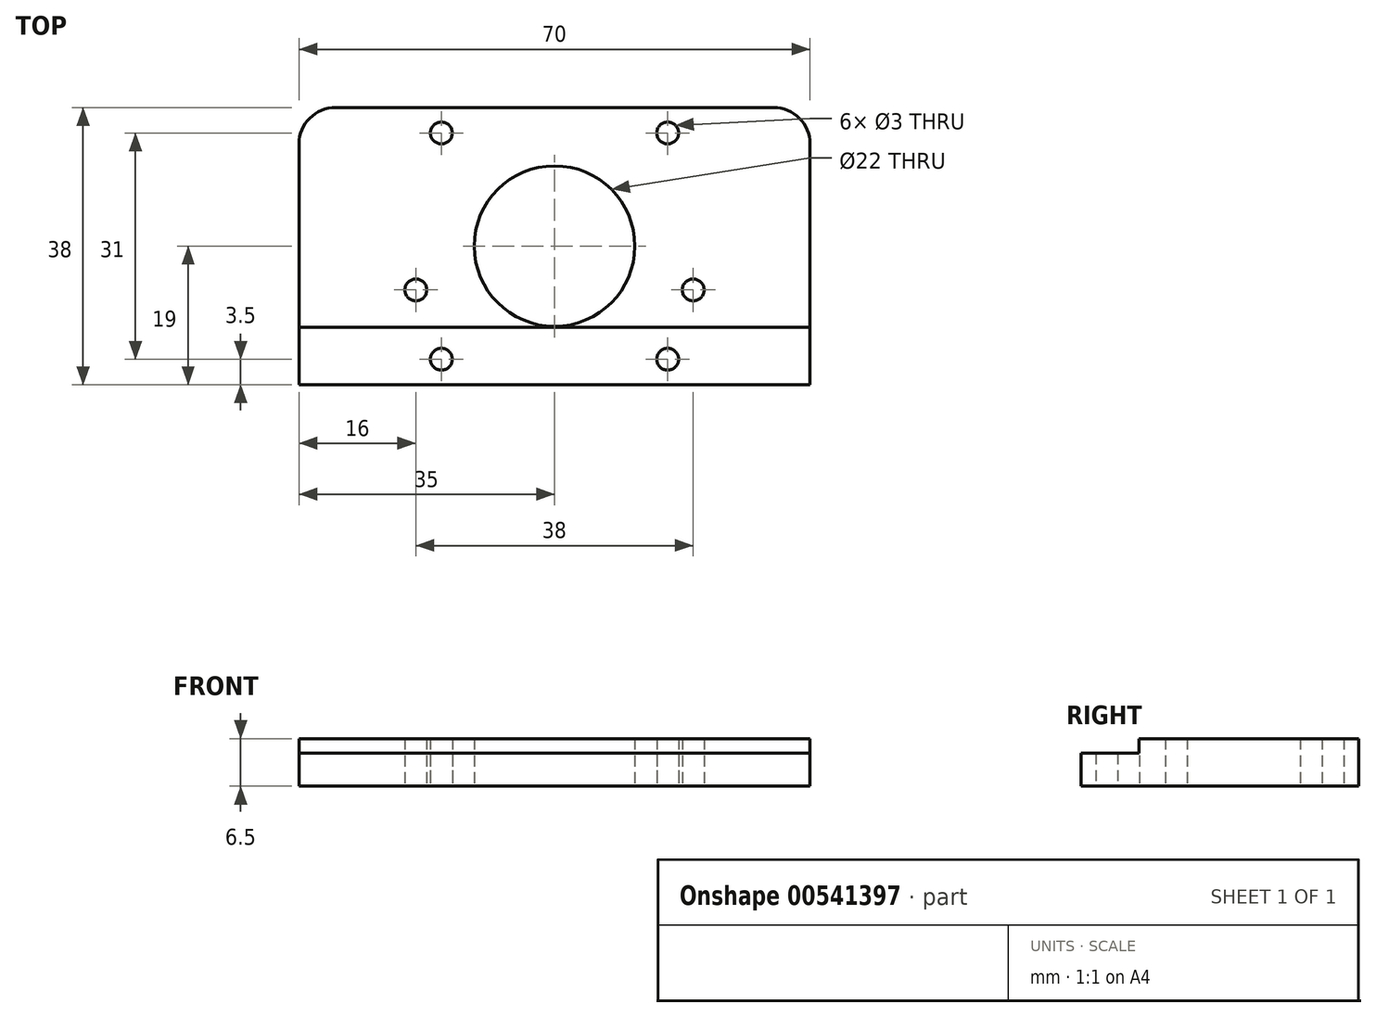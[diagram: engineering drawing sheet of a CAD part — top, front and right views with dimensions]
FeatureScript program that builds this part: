
annotation { "Feature Type Name" : "Feature", "Feature Type Description" : "" }
export const myFeature = defineFeature(function(context is Context, id is Id, definition is map)
    precondition{}
    {
        {
            var Q0;
            Q0=qCreatedBy(makeId("Top.planeOp"),FACE);
            var sketch = newSketch(context, id + "F0", { "sketchPlane" : qUnion([Q0])});
            skLineSegment(sketch, "E0.bottom", {"start": v(35, 19) * mm, "end": v(-35, 19) * mm});
            skLineSegment(sketch, "E0.top", {"start": v(35, -19) * mm, "end": v(-35, -19) * mm});
            skLineSegment(sketch, "E0.left", {"start": v(35, 19) * mm, "end": v(35, -19) * mm});
            skLineSegment(sketch, "E0.right", {"start": v(-35, 19) * mm, "end": v(-35, -19) * mm});
            skCircle(sketch, "E1", {"center": v(-15.5, 15.5) * mm, "radius": 1.5 * mm});
            skCircle(sketch, "E2", {"center": v(15.5, 15.5) * mm, "radius": 1.5 * mm});
            skCircle(sketch, "E3", {"center": v(-15.5, -15.5) * mm, "radius": 1.5 * mm});
            skCircle(sketch, "E4", {"center": v(15.5, -15.5) * mm, "radius": 1.5 * mm});
            skCircle(sketch, "E5", {"center": v(19, -6) * mm, "radius": 1.5 * mm});
            skCircle(sketch, "E6", {"center": v(-19, -6) * mm, "radius": 1.5 * mm});
            skCircle(sketch, "E7", {"center": v(0, 0) * mm, "radius": 11 * mm});
            skLineSegment(sketch, "E8", {"start": v(-15.5, 15.5) * mm, "end": v(15.5, 15.5) * mm, "construction": true});
            skLineSegment(sketch, "E9", {"start": v(-15.5, 15.5) * mm, "end": v(-15.5, -15.5) * mm, "construction": true});
            skLineSegment(sketch, "E10", {"start": v(15.5, -15.5) * mm, "end": v(-15.5, -15.5) * mm, "construction": true});
            skLineSegment(sketch, "E11", {"start": v(15.5, 15.5) * mm, "end": v(15.5, -15.5) * mm, "construction": true});
            skPoint(sketch, "E12.endSnap0", {"position": v(0, -19) * mm});
            skSolve(sketch);
        }
        {
            var Q0;
            Q0=makeQuery(id+"F0.imprint","IMPRINT",FACE,{"disambiguationData":[TD([[makeQuery(id+"F0.imprint","IMPRINT",EDGE,{"derivedFrom":sQuery(id+"F0.wireOp",EDGE,"E0.bottom")}),1.0]])]});
            var Q1;
            Q1=sQuery(id+"F0.wireOp",EDGE,"E0.bottom");
            var Q2;
            Q2=sQuery(id+"F0.wireOp",EDGE,"E0.right");
            var Q3;
            Q3=sQuery(id+"F0.wireOp",EDGE,"E0.top");
            var Q4;
            Q4=sQuery(id+"F0.wireOp",EDGE,"E0.left");
            extrude(context, id + "F1", {"entities" : qUnion([Q0]), "surfaceEntities" : qUnion([Q1, Q2, Q3, Q4]), "depth" : 6.5 * mm, "offsetDistance" : 25 * mm});
        }
        {
            var Q0;
            Q0=makeQuery(id+"F1.opExtrude","CAP_FACE",FACE,{"disambiguationData":[OSD([sQuery(id+"F0.wireOp",EDGE,"E0.bottom"),sQuery(id+"F0.wireOp",EDGE,"E0.top"),sQuery(id+"F0.wireOp",EDGE,"E0.left"),sQuery(id+"F0.wireOp",EDGE,"E0.right"),sQuery(id+"F0.wireOp",EDGE,"E1"),sQuery(id+"F0.wireOp",EDGE,"E2"),sQuery(id+"F0.wireOp",EDGE,"E3"),sQuery(id+"F0.wireOp",EDGE,"E4"),sQuery(id+"F0.wireOp",EDGE,"E5"),sQuery(id+"F0.wireOp",EDGE,"E6"),sQuery(id+"F0.wireOp",EDGE,"E7")])],"isStart":false});
            var sketch = newSketch(context, id + "F2", { "sketchPlane" : qUnion([Q0])});
            skLineSegment(sketch, "E13", {"start": v(-35, -11.1) * mm, "end": v(35, -11.1) * mm});
            skSolve(sketch);
        }
        {
            var Q0;
            Q0 = qSketchRegion(id + "F2", true);
            var Q1;
            {var subQ2=sQuery(id+"F2.wireOp",EDGE,"E13");Q1=makeQuery(id+"F2.imprint","IMPRINT",FACE,{"disambiguationData":[TD([[makeQuery(id+"F2.imprint","IMPRINT",EDGE,{"derivedFrom":subQ2}),-1.0]])]});}
            extrude(context, id + "F3", {"entities" : qUnion([Q0, Q1]), "operationType" : NewBodyOperationType.REMOVE, "oppositeDirection" : true, "depth" : 2 * mm, "offsetDistance" : 25 * mm});
        }
        {
            var Q0;
            Q0=makeQuery(id+"F1.opExtrude","SWEPT_EDGE",EDGE,{"disambiguationData":[OSD([sQuery(id+"F0.wireOp",EDGE,"E0.bottom"),sQuery(id+"F0.wireOp",EDGE,"E0.left")])]});
            var Q1;
            Q1=makeQuery(id+"F1.opExtrude","SWEPT_EDGE",EDGE,{"disambiguationData":[OSD([sQuery(id+"F0.wireOp",EDGE,"E0.bottom"),sQuery(id+"F0.wireOp",EDGE,"E0.right")])]});
            fillet(context, id + "F4", {"entities" : qUnion([Q0, Q1]), "radius" : 5 * mm, "tangentPropagation" : true, "allowEdgeOverflow" : false});
        }
    });
